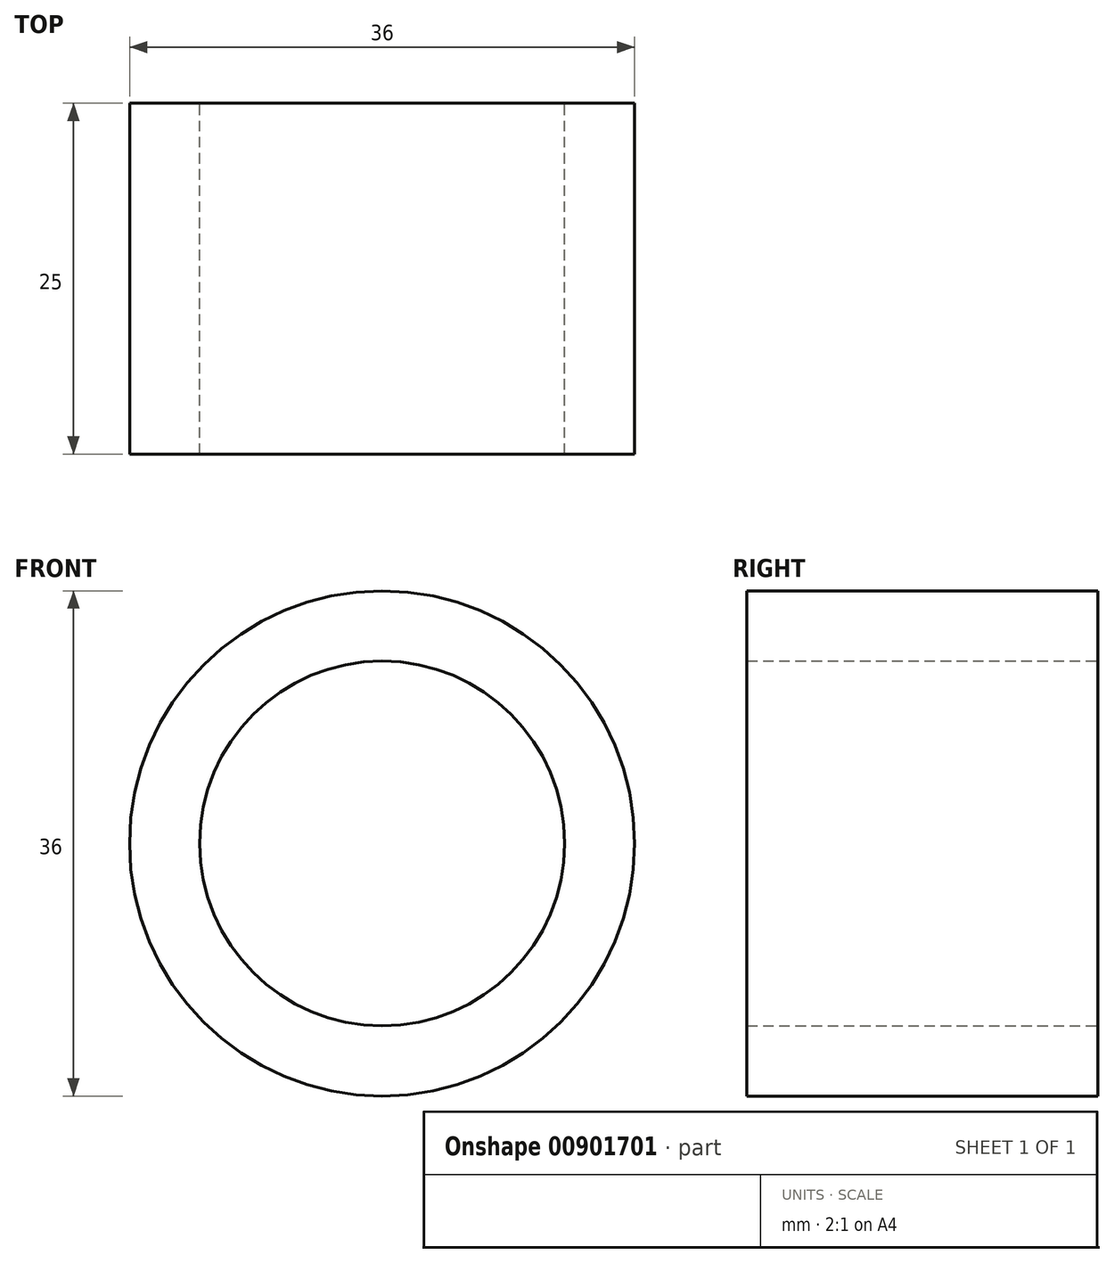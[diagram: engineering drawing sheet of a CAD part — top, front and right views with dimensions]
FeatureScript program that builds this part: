
annotation { "Feature Type Name" : "Feature", "Feature Type Description" : "" }
export const myFeature = defineFeature(function(context is Context, id is Id, definition is map)
    precondition{}
    {
        {
            var Q0;
            Q0=qCreatedBy(makeId("Front.planeOp"),FACE);
            var sketch = newSketch(context, id + "F0", { "sketchPlane" : qUnion([Q0])});
            skCircle(sketch, "E0", {"center": v(0, 0) * mm, "radius": 13 * mm});
            skCircle(sketch, "E1.0", {"center": v(0, 0) * mm, "radius": 18 * mm});
            skSolve(sketch);
        }
        {
            var Q0;
            Q0=makeQuery(id+"F0.imprint","IMPRINT",FACE,{"disambiguationData":[TD([[makeQuery(id+"F0.imprint","IMPRINT",EDGE,{"derivedFrom":sQuery(id+"F0.wireOp",EDGE,"E0")}),-1.0]])]});
            var Q1;
            Q1 = qSketchRegion(id + "F0", true);
            extrude(context, id + "F1", {"entities" : qUnion([Q0, Q1]), "depth" : 25 * mm, "offsetDistance" : 25 * mm});
        }
    });
